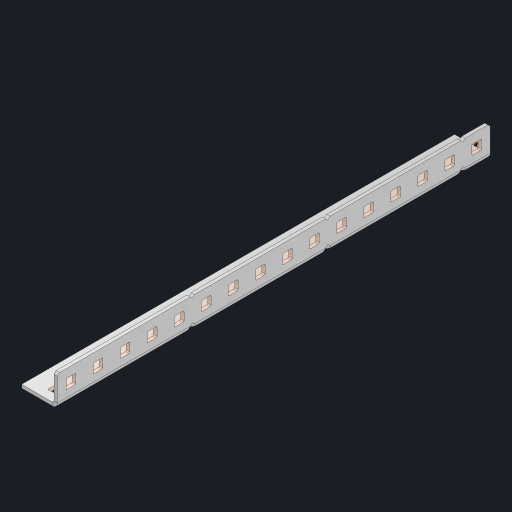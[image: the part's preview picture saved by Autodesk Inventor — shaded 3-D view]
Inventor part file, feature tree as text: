
AUTODESK INVENTOR PART (.ipt)
format: ipt  version: 2023 (Build 270158000, 158)  size: 700,928 bytes
history: native  units: in
note: dims shown in document units (in); Inventor stores cm internally (conversion verified against a paired STEP export)
features: other x37, extrude x31, sheet_metal_op x10, sketch x8, mirror x1, pattern_linear x1, chamfer x1
ambient origin geometry x8: Origin, YZ Plane, XZ Plane, XY Plane, X Axis, Y Axis, Z Axis, Center Point
bodies: Solid1 (feature_tree), Body (feature_tree)
feature tree (89):
  other  "Flange Pattern Plane"
  sheet_metal_op  "Flange Pattern"
  sheet_metal_op  "Body Pattern"
  other  "Arc Length"
  mirror  "Notch Mirror"
  pattern_linear  "Notch Pattern"  Spacing1=0.25in  [1 undecoded]
  chamfer  "End Chamfer"
  extrude  "Half Cut"  Depth=0.0625in
  sketch  "Sketch1"  dims[d0=1.5in]
  other  "Plate1"
  sketch  "Sketch2"  dims[d1=8.0in]
  other  "Plate2"
  sheet_metal_op  "Bend1"
  sheet_metal_op  "Corner1"
  sketch  "Sketch3"  dims[d2=0.0625in]
  other  "Flange Pattern Sketch"
  sketch  "Sketch7"  dims[d3=0.0625in]
  other  "Srf1"
  other  "Srf2"
  sketch  "Sketch8"  dims[d4=0.0312in]
  sketch  "Sketch9"  dims[d5=0.125in]
  other  "Srf91"
  sheet_metal_op  "Body Pattern Sketch"
  other  "Srf92"
  sketch  "Sketch13"  dims[d6=0.0625in]
  sketch  "Sketch14"  dims[d7=0.5in d8=90.0deg d9=0.0312in d10=0.25in d11=0.0625in d12=0.0625in d16=0.182in d17=0.02in d18=0.0625in d19=0.0in d20=0.25in d21=0.25in d46=0.172in d47=1.0in d48=0.0in d49=0.182in d50=0.02in d51=0.25in d52=0.25in d53=0.0625in d54=0.0in d55=0.172in d56=1.0in d57=0.0in d60=6.2992in d62=0.5in d63=0.3937in d65=0.5in d85=0.1473in d86=0.1782in d88=0.04in d89=0.0625in d90=0.0in d91=0.04in d92=0.0491in d95=2.5in d96=0.04in d97=0.25in d98=45.0deg d101=0.0in d102=2.497in d131=0.5in d132=6.2992in d134=0.5in d139=0.5in]
  other  "Srf856"
  other  "Srf1310"
  other  "Srf1311"
  other  "Srf1312"
  other  "Srf1376"
  other  "Srf1377"
  other  "Srf1728"
  other  "Srf1755"
  other  "Srf1878"
  other  "Srf1879"
  other  "Srf1880"
  other  "Srf1881"
  other  "Srf1882"
  other  "Srf1883"
  other  "Srf1884"
  other  "Srf1885"
  other  "Srf1886"
  other  "Srf1887"
  other  "Srf1942"
  other  "Srf1943"
  other  "Srf1944"
  other  "Srf1945"
  other  "Srf1946"
  other  "Srf1947"
  other  "Srf1948"
  other  "Srf1949"
  other  "Srf1950"
  other  "Srf1951"
  sheet_metal_op  "Flange Stamp"
  sheet_metal_op  "Flange Circle"
  sheet_metal_op  "Body Stamp"
  sheet_metal_op  "Body Circle"
  sheet_metal_op  "Notch"
  extrude  "ExtrusionSrf2"  Depth=0.0625in
  extrude  "ExtrusionSrf92"  Depth=0.5in
  extrude  "ExtrusionSrf856"  Depth=0.02in
  extrude  "ExtrusionSrf1310"  Depth=0.0625in
  extrude  "ExtrusionSrf1311"  TaperAngle=0.0deg  [1 undecoded]
  extrude  "ExtrusionSrf1312"  Depth=0.5in
  extrude  "ExtrusionSrf1376"  Depth=0.5in
  extrude  "ExtrusionSrf1377"  Depth=0.5in
  extrude  "ExtrusionSrf1728"  Depth=0.5in TaperAngle=0.0deg
  extrude  "ExtrusionSrf1755"  Depth=0.5in
  extrude  "ExtrusionSrf1878"  Depth=0.02in
  extrude  "ExtrusionSrf1879"  Depth=0.5in
  extrude  "ExtrusionSrf1880"  Depth=0.5in
  extrude  "ExtrusionSrf1881"  Depth=0.0625in
  extrude  "ExtrusionSrf1882"  TaperAngle=0.0deg  [1 undecoded]
  extrude  "ExtrusionSrf1883"  Depth=0.5in
  extrude  "ExtrusionSrf1884"  Depth=0.5in TaperAngle=0.0deg
  extrude  "ExtrusionSrf1885"  Depth=0.5in
  extrude  "ExtrusionSrf1886"  Depth=0.5in
  extrude  "ExtrusionSrf1887"  Depth=0.5in
  extrude  "ExtrusionSrf1942"  Depth=0.5in
  extrude  "ExtrusionSrf1943"  Depth=0.5in
  extrude  "ExtrusionSrf1944"  Depth=0.0625in
  extrude  "ExtrusionSrf1945"  TaperAngle=0.0deg  [1 undecoded]
  extrude  "ExtrusionSrf1946"  Depth=0.5in
  extrude  "ExtrusionSrf1947"  Depth=0.5in
  extrude  "ExtrusionSrf1948"  Depth=0.5in
  extrude  "ExtrusionSrf1949"  Depth=0.5in TaperAngle=45.0deg
  extrude  "ExtrusionSrf1950"  TaperAngle=0.0deg  [1 undecoded]
  extrude  "ExtrusionSrf1951"  Depth=0.5in
note: 5 required parameter values undecoded (feature->parameter linkage not recoverable at this tier; creation-order binding heuristic only, values carry confidence <= 0.55)
